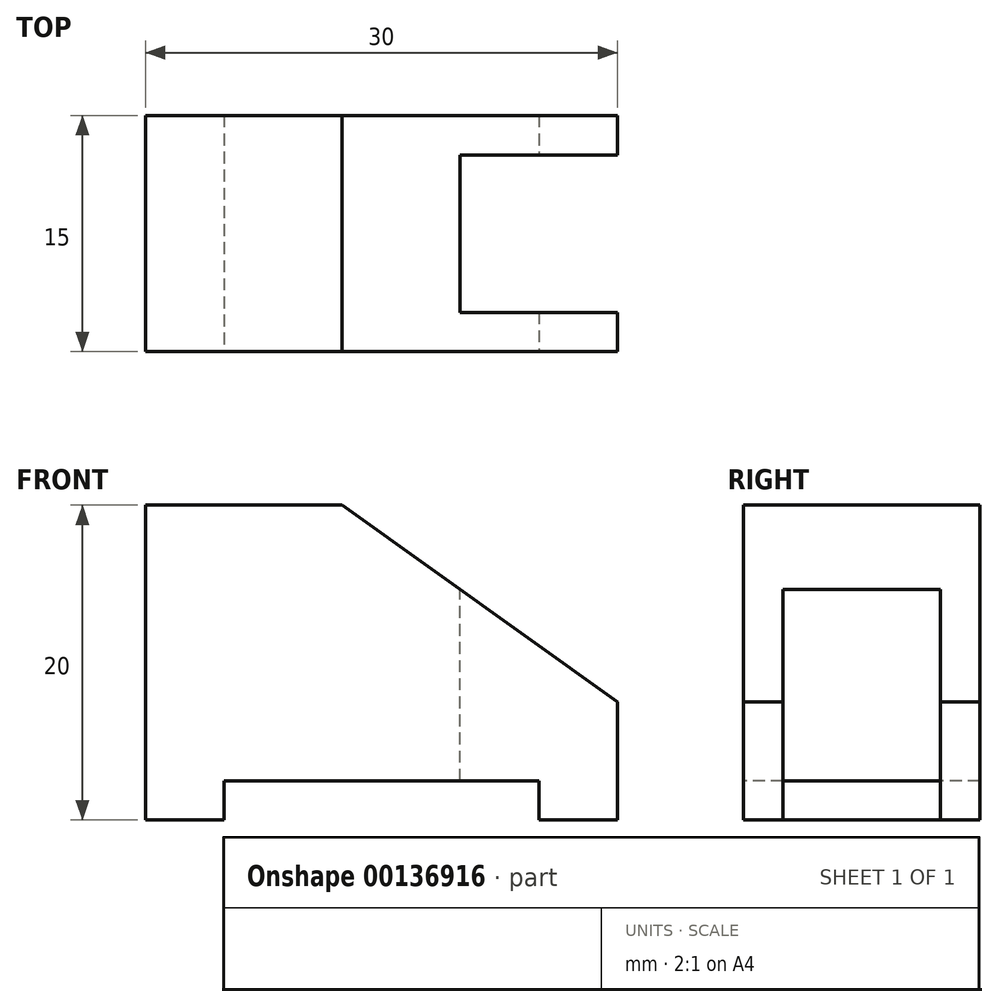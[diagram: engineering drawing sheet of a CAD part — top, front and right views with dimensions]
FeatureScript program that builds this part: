
annotation { "Feature Type Name" : "Feature", "Feature Type Description" : "" }
export const myFeature = defineFeature(function(context is Context, id is Id, definition is map)
    precondition{}
    {
        {
            var Q0;
            Q0=qCreatedBy(makeId("Top.planeOp"),FACE);
            var sketch = newSketch(context, id + "F0", { "sketchPlane" : qUnion([Q0])});
            skLineSegment(sketch, "E0.bottom", {"start": v(0, 0) * mm, "end": v(12.5, 0) * mm});
            skLineSegment(sketch, "E0.top", {"start": v(0, 15) * mm, "end": v(12.5, 15) * mm});
            skLineSegment(sketch, "E0.left", {"start": v(0, 0) * mm, "end": v(0, 15) * mm});
            skLineSegment(sketch, "E0.right", {"start": v(12.5, 0) * mm, "end": v(12.5, 15) * mm});
            skLineSegment(sketch, "E1.bottom", {"start": v(12.5, 15) * mm, "end": v(20, 15) * mm});
            skLineSegment(sketch, "E1.top", {"start": v(12.5, 0) * mm, "end": v(20, 0) * mm});
            skLineSegment(sketch, "E1.left", {"start": v(12.5, 15) * mm, "end": v(12.5, 0) * mm});
            skLineSegment(sketch, "E1.right", {"start": v(20, 12.5) * mm, "end": v(20, 2.5) * mm});
            skLineSegment(sketch, "E2.bottom", {"start": v(20, 15) * mm, "end": v(30, 15) * mm});
            skLineSegment(sketch, "E2.top", {"start": v(20, 12.5) * mm, "end": v(30, 12.5) * mm});
            skLineSegment(sketch, "E2.right", {"start": v(30, 15) * mm, "end": v(30, 12.5) * mm});
            skLineSegment(sketch, "E3.bottom", {"start": v(20, 0) * mm, "end": v(30, 0) * mm});
            skLineSegment(sketch, "E3.top", {"start": v(20, 2.5) * mm, "end": v(30, 2.5) * mm});
            skLineSegment(sketch, "E3.right", {"start": v(30, 0) * mm, "end": v(30, 2.5) * mm});
            skSolve(sketch);
        }
        {
            var Q0;
            Q0=makeQuery(id+"F0.imprint","IMPRINT",FACE,{"disambiguationData":[TD([[makeQuery(id+"F0.imprint","IMPRINT",EDGE,{"derivedFrom":sQuery(id+"F0.wireOp",EDGE,"E0.bottom")}),1.0]])]});
            extrude(context, id + "F1", {"entities" : qUnion([Q0]), "oppositeDirection" : true, "depth" : 20 * mm});
        }
        {
            var Q0;
            Q0=makeQuery(id+"F0.imprint","IMPRINT",FACE,{"disambiguationData":[TD([[makeQuery(id+"F0.imprint","IMPRINT",EDGE,{"derivedFrom":sQuery(id+"F0.wireOp",EDGE,"E1.bottom")}),-1.0]])]});
            extrude(context, id + "F2", {"entities" : qUnion([Q0]), "operationType" : NewBodyOperationType.ADD, "oppositeDirection" : true, "depth" : 20 * mm});
        }
        {
            var Q0;
            Q0=makeQuery(id+"F2.boolean.opBoolean","MERGE",FACE,{"derivedFrom":[makeQuery(id+"F1.opExtrude","SWEPT_FACE",FACE,{"disambiguationData":[OSD([sQuery(id+"F0.wireOp",EDGE,"E0.bottom")])]}),makeQuery(id+"F2.opExtrude","SWEPT_FACE",FACE,{"disambiguationData":[OSD([sQuery(id+"F0.wireOp",EDGE,"E1.top"),sQuery(id+"F0.wireOp",EDGE,"E3.bottom")])]})]});
            var sketch = newSketch(context, id + "F3", { "sketchPlane" : qUnion([Q0])});
            skLineSegment(sketch, "E4.bottom", {"start": v(0, 0) * mm, "end": v(30, 0) * mm});
            skLineSegment(sketch, "E4.top", {"start": v(0, -20) * mm, "end": v(5, -20) * mm});
            skLineSegment(sketch, "E4.left", {"start": v(0, 0) * mm, "end": v(0, -20) * mm});
            skLineSegment(sketch, "E4.right", {"start": v(30, 0) * mm, "end": v(30, -20) * mm});
            skLineSegment(sketch, "E5.top", {"start": v(5, -17.5) * mm, "end": v(25, -17.5) * mm});
            skLineSegment(sketch, "E5.left", {"start": v(5, -20) * mm, "end": v(5, -17.5) * mm});
            skLineSegment(sketch, "E5.right", {"start": v(25, -20) * mm, "end": v(25, -17.5) * mm});
            skLineSegment(sketch, "E6.trimOffspring", {"start": v(25, -20) * mm, "end": v(30, -20) * mm});
            skLineSegment(sketch, "E7", {"start": v(5, -20) * mm, "end": v(25, -20) * mm});
            skPoint(sketch, "E8", {"position": v(12.5, 0) * mm});
            skPoint(sketch, "E9", {"position": v(30, -12.5) * mm});
            skLineSegment(sketch, "E10", {"start": v(12.5, 0) * mm, "end": v(30, -12.5) * mm});
            skSolve(sketch);
        }
        {
            var Q0;
            {var subQ3=sQuery(id+"F3.wireOp",EDGE,"E10");Q0=makeQuery(id+"F3.imprint","IMPRINT",FACE,{"disambiguationData":[TD([[makeQuery(id+"F3.imprint","IMPRINT",EDGE,{"derivedFrom":subQ3}),1.0]])]});}
            extrude(context, id + "F4", {"entities" : qUnion([Q0]), "operationType" : NewBodyOperationType.REMOVE, "endBound" : BoundingType.THROUGH_ALL, "oppositeDirection" : true, "depth" : 15.65 * mm});
        }
        {
            var Q0;
            Q0=makeQuery(id+"F3.imprint","IMPRINT",FACE,{"disambiguationData":[TD([[makeQuery(id+"F3.imprint","IMPRINT",EDGE,{"derivedFrom":sQuery(id+"F3.wireOp",EDGE,"E5.top")}),-1.0]])]});
            extrude(context, id + "F5", {"entities" : qUnion([Q0]), "operationType" : NewBodyOperationType.REMOVE, "endBound" : BoundingType.THROUGH_ALL, "oppositeDirection" : true, "depth" : 25 * mm});
        }
    });
